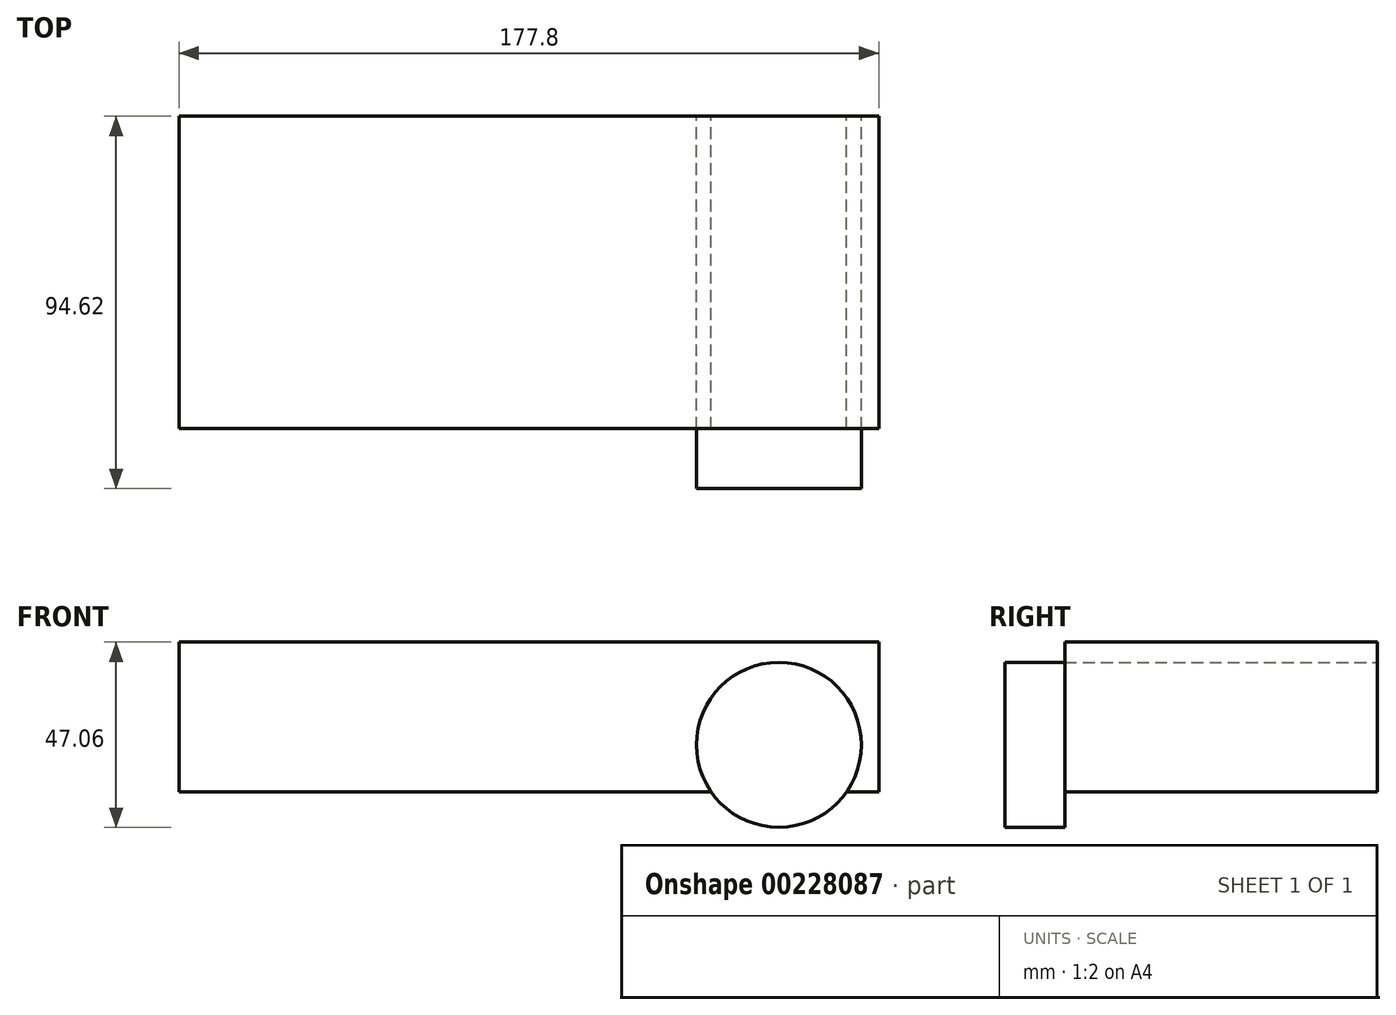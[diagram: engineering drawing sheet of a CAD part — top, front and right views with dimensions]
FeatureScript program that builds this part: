
annotation { "Feature Type Name" : "Feature", "Feature Type Description" : "" }
export const myFeature = defineFeature(function(context is Context, id is Id, definition is map)
    precondition{}
    {
        {
            var Q0;
            Q0=qCreatedBy(makeId("Front.planeOp"),FACE);
            var sketch = newSketch(context, id + "F0", { "sketchPlane" : qUnion([Q0])});
            skLineSegment(sketch, "E0.bottom", {"start": v(88.9, -19.05) * mm, "end": v(-88.9, -19.05) * mm});
            skLineSegment(sketch, "E0.top", {"start": v(88.9, 19.05) * mm, "end": v(-88.9, 19.05) * mm});
            skLineSegment(sketch, "E0.left", {"start": v(88.9, -19.05) * mm, "end": v(88.9, 19.05) * mm});
            skLineSegment(sketch, "E0.right", {"start": v(-88.9, -19.05) * mm, "end": v(-88.9, 19.05) * mm});
            skPoint(sketch, "E0.middle", {"position": v(0, 0) * mm});
            skLineSegment(sketch, "E1", {"start": v(-114.54, -38.1) * mm, "end": v(110.15, -38.1) * mm, "construction": true});
            skCircle(sketch, "E2", {"center": v(63.5, -7.05) * mm, "radius": 20.96 * mm});
            skSolve(sketch);
        }
        {
            var Q0;
            Q0=makeQuery(id+"F0.imprint","IMPRINT",FACE,{"disambiguationData":[TD([[makeQuery(id+"F0.imprint","IMPRINT",EDGE,{"derivedFrom":sQuery(id+"F0.wireOp",EDGE,"E0.top")}),1.0]])]});
            var Q1;
            {var subQ0=sQuery(id+"F0.wireOp",EDGE,"E2");var subQ1=sQuery(id+"F0.wireOp",EDGE,"E0.bottom");var subQ2=makeQuery(id+"F0.imprint","INTERSECT",VERTEX,{"disambiguationData":[OD(0.0)],"derivedFrom":[subQ1,subQ0]});Q1=makeQuery(id+"F0.imprint","IMPRINT",FACE,{"disambiguationData":[TD([[makeQuery(id+"F0.imprint","IMPRINT",EDGE,{"disambiguationData":[TD([[subQ2,-1.0]])],"derivedFrom":subQ1}),-1.0]])]});}
            extrude(context, id + "F1", {"entities" : qUnion([Q0, Q1]), "endBound" : BoundingType.SYMMETRIC, "depth" : 79.38 * mm});
        }
        {
            var Q0;
            Q0=makeQuery(id+"F1.opExtrude","CAP_FACE",FACE,{"disambiguationData":[OSD([sQuery(id+"F0.wireOp",EDGE,"E0.bottom"),sQuery(id+"F0.wireOp",EDGE,"E0.top"),sQuery(id+"F0.wireOp",EDGE,"E0.left"),sQuery(id+"F0.wireOp",EDGE,"E0.right")])],"isStart":false});
            var sketch = newSketch(context, id + "F2", { "sketchPlane" : qUnion([Q0])});
            skCircle(sketch, "E3.0", {"center": v(63.5, -7.05) * mm, "radius": 20.96 * mm});
            skSolve(sketch);
        }
        {
            var Q0;
            Q0 = qSketchRegion(id + "F2", true);
            extrude(context, id + "F3", {"entities" : qUnion([Q0]), "operationType" : NewBodyOperationType.ADD, "depth" : 15.24 * mm});
        }
    });
